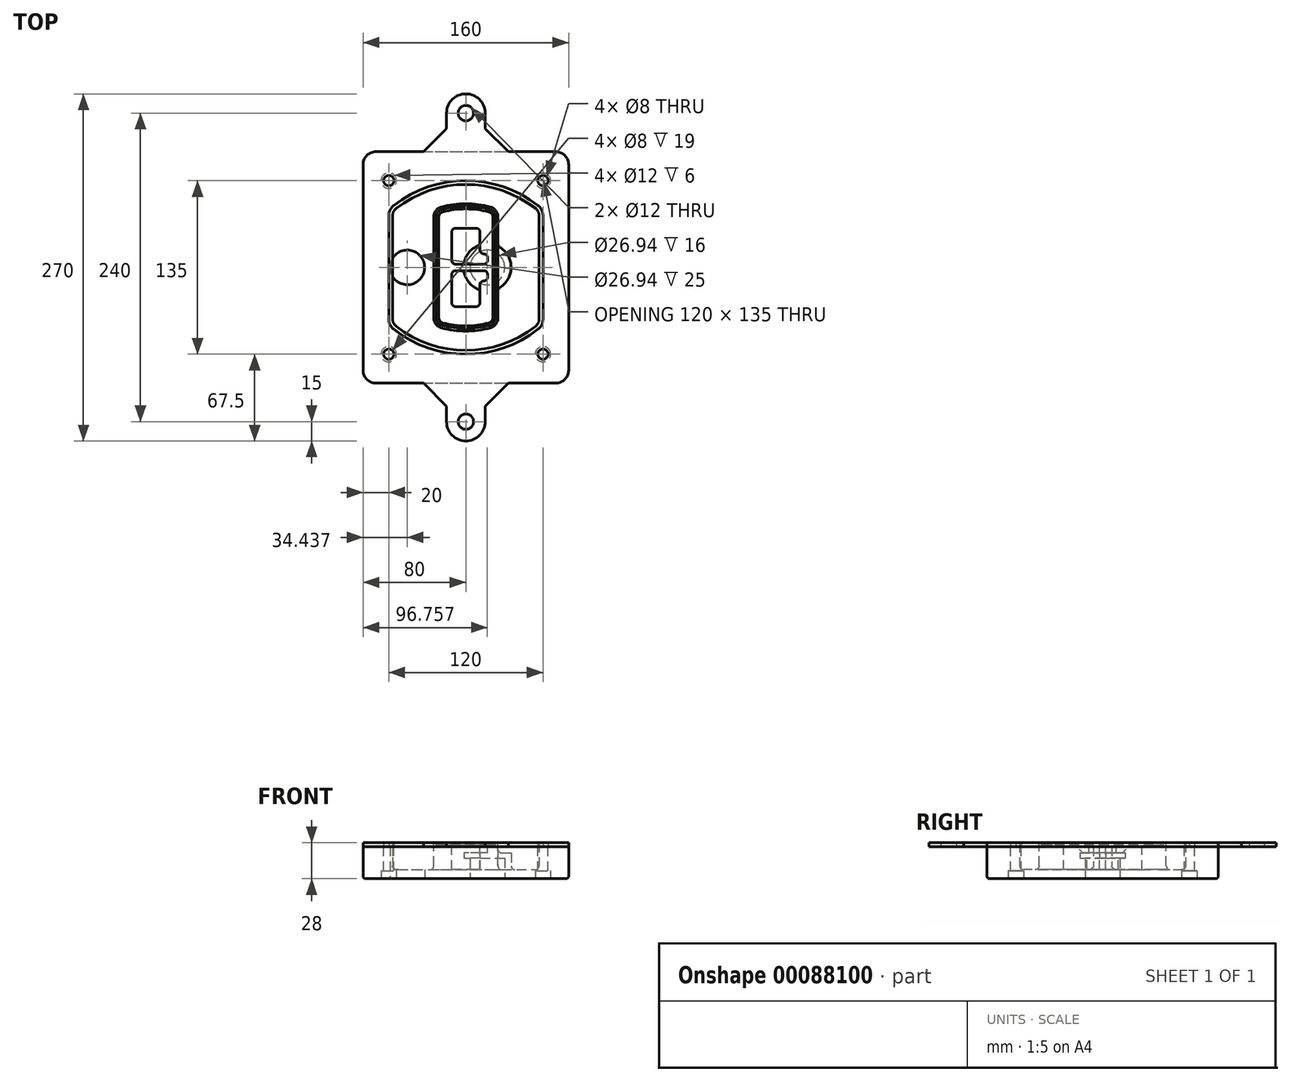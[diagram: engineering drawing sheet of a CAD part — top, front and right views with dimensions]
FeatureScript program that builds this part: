
annotation { "Feature Type Name" : "Feature", "Feature Type Description" : "" }
export const myFeature = defineFeature(function(context is Context, id is Id, definition is map)
    precondition{}
    {
        {
            var Q0;
            Q0=qCreatedBy(makeId("Top.planeOp"),FACE);
            var sketch = newSketch(context, id + "F0", { "sketchPlane" : qUnion([Q0])});
            skPoint(sketch, "E0.rect.middle", {"position": v(0, 0) * mm});
            skLineSegment(sketch, "E1.bottom", {"start": v(-70, -90) * mm, "end": v(70, -90) * mm});
            skLineSegment(sketch, "E1.top", {"start": v(-70, 90) * mm, "end": v(70, 90) * mm});
            skLineSegment(sketch, "E1.left", {"start": v(-80, -80) * mm, "end": v(-80, 80) * mm});
            skLineSegment(sketch, "E1.right", {"start": v(80, -80) * mm, "end": v(80, 80) * mm});
            skLineSegment(sketch, "E2", {"start": v(-80, 90) * mm, "end": v(80, -90) * mm, "construction": true});
            skLineSegment(sketch, "E3", {"start": v(80, 90) * mm, "end": v(-80, -90) * mm, "construction": true});
            skCircle(sketch, "E4", {"center": v(-60, 67.5) * mm, "radius": 4 * mm});
            skCircle(sketch, "E5", {"center": v(60, 67.5) * mm, "radius": 4 * mm});
            skCircle(sketch, "E6", {"center": v(60, -67.5) * mm, "radius": 4 * mm});
            skCircle(sketch, "E7", {"center": v(-60, -67.5) * mm, "radius": 4 * mm});
            skLineSegment(sketch, "E8", {"start": v(-60, 67.5) * mm, "end": v(60, 67.5) * mm, "construction": true});
            skLineSegment(sketch, "E9", {"start": v(60, 67.5) * mm, "end": v(60, -67.5) * mm, "construction": true});
            skLineSegment(sketch, "E10", {"start": v(60, -67.5) * mm, "end": v(-60, -67.5) * mm, "construction": true});
            skLineSegment(sketch, "E11", {"start": v(-60, -67.5) * mm, "end": v(-60, 67.5) * mm, "construction": true});
            skLineSegment(sketch, "E12", {"start": v(-60, 40.3) * mm, "end": v(-60, -40.3) * mm});
            skLineSegment(sketch, "E13", {"start": v(60, 40.3) * mm, "end": v(60, -40.3) * mm});
            skArc(sketch, "E14", {"start": v(56.15, 48.18) * mm, "mid": v(0, 67.5) * mm, "end": v(-56.15, 48.18) * mm});
            skArc(sketch, "E15", {"start": v(-56.15, -48.18) * mm, "mid": v(0, -67.5) * mm, "end": v(56.15, -48.18) * mm});
            skLineSegment(sketch, "E16", {"start": v(-60, 0) * mm, "end": v(60, 0) * mm, "construction": true});
            skPoint(sketch, "E17.visualSharp", {"position": v(-60, -45) * mm});
            skArc(sketch, "E17.filletArc", {"start": v(-60, -40.3) * mm, "mid": v(-58.99, -44.68) * mm, "end": v(-56.15, -48.18) * mm});
            skPoint(sketch, "E18.visualSharp", {"position": v(-60, 45) * mm});
            skArc(sketch, "E18.filletArc", {"start": v(-56.15, 48.18) * mm, "mid": v(-58.99, 44.68) * mm, "end": v(-60, 40.3) * mm});
            skPoint(sketch, "E19.visualSharp", {"position": v(60, 45) * mm});
            skArc(sketch, "E19.filletArc", {"start": v(60, 40.3) * mm, "mid": v(58.99, 44.68) * mm, "end": v(56.15, 48.18) * mm});
            skPoint(sketch, "E20.visualSharp", {"position": v(60, -45) * mm});
            skArc(sketch, "E20.filletArc", {"start": v(56.15, -48.18) * mm, "mid": v(58.99, -44.68) * mm, "end": v(60, -40.3) * mm});
            skPoint(sketch, "E21.visualSharp", {"position": v(-80, 90) * mm});
            skArc(sketch, "E21.filletArc", {"start": v(-70, 90) * mm, "mid": v(-77.07, 87.07) * mm, "end": v(-80, 80) * mm});
            skPoint(sketch, "E22.visualSharp", {"position": v(80, 90) * mm});
            skArc(sketch, "E22.filletArc", {"start": v(80, 80) * mm, "mid": v(77.07, 87.07) * mm, "end": v(70, 90) * mm});
            skPoint(sketch, "E23.visualSharp", {"position": v(80, -90) * mm});
            skArc(sketch, "E23.filletArc", {"start": v(70, -90) * mm, "mid": v(77.07, -87.07) * mm, "end": v(80, -80) * mm});
            skPoint(sketch, "E24.visualSharp", {"position": v(-80, -90) * mm});
            skArc(sketch, "E24.filletArc", {"start": v(-80, -80) * mm, "mid": v(-77.07, -87.07) * mm, "end": v(-70, -90) * mm});
            skArc(sketch, "E25.0", {"start": v(57, 40.3) * mm, "mid": v(56.3, 43.36) * mm, "end": v(54.3, 45.81) * mm});
            skLineSegment(sketch, "E25.1", {"start": v(57, 40.3) * mm, "end": v(57, -40.3) * mm});
            skArc(sketch, "E25.2", {"start": v(54.3, -45.81) * mm, "mid": v(56.3, -43.36) * mm, "end": v(57, -40.3) * mm});
            skArc(sketch, "E25.3", {"start": v(-54.3, -45.81) * mm, "mid": v(0, -64.5) * mm, "end": v(54.3, -45.81) * mm});
            skArc(sketch, "E25.4", {"start": v(-57, -40.3) * mm, "mid": v(-56.3, -43.36) * mm, "end": v(-54.3, -45.81) * mm});
            skArc(sketch, "E25.5", {"start": v(54.3, 45.81) * mm, "mid": v(0, 64.5) * mm, "end": v(-54.3, 45.81) * mm});
            skLineSegment(sketch, "E25.6", {"start": v(-57, 40.3) * mm, "end": v(-57, -40.3) * mm});
            skArc(sketch, "E25.7", {"start": v(-54.3, 45.81) * mm, "mid": v(-56.3, 43.36) * mm, "end": v(-57, 40.3) * mm});
            skArc(sketch, "E26.0", {"start": v(-58.62, 51.33) * mm, "mid": v(-62.58, 46.43) * mm, "end": v(-64, 40.3) * mm});
            skArc(sketch, "E26.1", {"start": v(58.62, 51.33) * mm, "mid": v(0, 71.5) * mm, "end": v(-58.62, 51.33) * mm});
            skArc(sketch, "E26.2", {"start": v(64, 40.3) * mm, "mid": v(62.58, 46.43) * mm, "end": v(58.62, 51.33) * mm});
            skLineSegment(sketch, "E26.3", {"start": v(64, 40.3) * mm, "end": v(64, -40.3) * mm});
            skArc(sketch, "E26.4", {"start": v(58.62, -51.33) * mm, "mid": v(62.58, -46.43) * mm, "end": v(64, -40.3) * mm});
            skLineSegment(sketch, "E26.5", {"start": v(-64, 40.3) * mm, "end": v(-64, -40.3) * mm});
            skArc(sketch, "E26.6", {"start": v(-58.62, -51.33) * mm, "mid": v(0, -71.5) * mm, "end": v(58.62, -51.33) * mm});
            skArc(sketch, "E26.7", {"start": v(-64, -40.3) * mm, "mid": v(-62.58, -46.43) * mm, "end": v(-58.62, -51.33) * mm});
            skSolve(sketch);
        }
        {
            var Q0;
            Q0=makeQuery(id+"F0.imprint","IMPRINT",FACE,{"disambiguationData":[TD([[makeQuery(id+"F0.imprint","IMPRINT",EDGE,{"derivedFrom":sQuery(id+"F0.wireOp",EDGE,"E1.bottom")}),1.0]])]});
            var Q1;
            Q1=makeQuery(id+"F0.imprint","IMPRINT",FACE,{"disambiguationData":[TD([[makeQuery(id+"F0.imprint","IMPRINT",EDGE,{"derivedFrom":sQuery(id+"F0.wireOp",EDGE,"E12")}),1.0]])]});
            var Q2;
            Q2=makeQuery(id+"F0.imprint","IMPRINT",FACE,{"disambiguationData":[TD([[makeQuery(id+"F0.imprint","IMPRINT",EDGE,{"derivedFrom":sQuery(id+"F0.wireOp",EDGE,"E25.0")}),1.0]])]});
            var Q3;
            Q3=makeQuery(id+"F0.imprint","IMPRINT",FACE,{"disambiguationData":[TD([[makeQuery(id+"F0.imprint","IMPRINT",EDGE,{"derivedFrom":sQuery(id+"F0.wireOp",EDGE,"E12")}),-1.0]])]});
            extrude(context, id + "F1", {"entities" : qUnion([Q0, Q1, Q2, Q3]), "oppositeDirection" : true, "depth" : 25 * mm});
        }
        {
            var Q0;
            Q0=makeQuery(id+"F0.imprint","IMPRINT",FACE,{"disambiguationData":[TD([[makeQuery(id+"F0.imprint","IMPRINT",EDGE,{"derivedFrom":sQuery(id+"F0.wireOp",EDGE,"E12")}),1.0]])]});
            extrude(context, id + "F2", {"entities" : qUnion([Q0]), "operationType" : NewBodyOperationType.ADD, "depth" : 3 * mm});
        }
        {
            var Q0;
            Q0=makeQuery(id+"F0.imprint","IMPRINT",FACE,{"disambiguationData":[TD([[makeQuery(id+"F0.imprint","IMPRINT",EDGE,{"derivedFrom":sQuery(id+"F0.wireOp",EDGE,"E25.0")}),1.0]])]});
            extrude(context, id + "F3", {"entities" : qUnion([Q0]), "operationType" : NewBodyOperationType.REMOVE, "oppositeDirection" : true, "depth" : 18 * mm});
        }
        {
            var Q0;
            Q0=makeQuery(id+"F2.opExtrude","CAP_FACE",FACE,{"disambiguationData":[OSD([sQuery(id+"F0.wireOp",EDGE,"E12"),sQuery(id+"F0.wireOp",EDGE,"E13"),sQuery(id+"F0.wireOp",EDGE,"E14"),sQuery(id+"F0.wireOp",EDGE,"E15"),sQuery(id+"F0.wireOp",EDGE,"E17.filletArc"),sQuery(id+"F0.wireOp",EDGE,"E18.filletArc"),sQuery(id+"F0.wireOp",EDGE,"E19.filletArc"),sQuery(id+"F0.wireOp",EDGE,"E20.filletArc"),sQuery(id+"F0.wireOp",EDGE,"E25.0"),sQuery(id+"F0.wireOp",EDGE,"E25.1"),sQuery(id+"F0.wireOp",EDGE,"E25.2"),sQuery(id+"F0.wireOp",EDGE,"E25.3"),sQuery(id+"F0.wireOp",EDGE,"E25.4"),sQuery(id+"F0.wireOp",EDGE,"E25.5"),sQuery(id+"F0.wireOp",EDGE,"E25.6"),sQuery(id+"F0.wireOp",EDGE,"E25.7")])],"isStart":false});
            var sketch = newSketch(context, id + "F4", { "sketchPlane" : qUnion([Q0])});
            skArc(sketch, "E27.0", {"start": v(-19.08, -46.97) * mm, "mid": v(0, -49.5) * mm, "end": v(19.08, -46.97) * mm});
            skArc(sketch, "E28.0", {"start": v(19.08, 46.97) * mm, "mid": v(0, 49.5) * mm, "end": v(-19.08, 46.97) * mm});
            skLineSegment(sketch, "E29", {"start": v(-25, 39.25) * mm, "end": v(-25, -39.25) * mm});
            skLineSegment(sketch, "E30", {"start": v(25, 39.25) * mm, "end": v(25, -39.25) * mm});
            skLineSegment(sketch, "E31", {"start": v(-25, 45.1) * mm, "end": v(25, 45.1) * mm, "construction": true});
            skLineSegment(sketch, "E32", {"start": v(-25, -45.1) * mm, "end": v(25, -45.1) * mm, "construction": true});
            skPoint(sketch, "E33.visualSharp", {"position": v(-25, 45.1) * mm});
            skArc(sketch, "E33.filletArc", {"start": v(-19.08, 46.97) * mm, "mid": v(-23.35, 44.11) * mm, "end": v(-25, 39.25) * mm});
            skPoint(sketch, "E34.visualSharp", {"position": v(25, 45.1) * mm});
            skArc(sketch, "E34.filletArc", {"start": v(25, 39.25) * mm, "mid": v(23.35, 44.11) * mm, "end": v(19.08, 46.97) * mm});
            skPoint(sketch, "E35.visualSharp", {"position": v(25, -45.1) * mm});
            skArc(sketch, "E35.filletArc", {"start": v(19.08, -46.97) * mm, "mid": v(23.35, -44.11) * mm, "end": v(25, -39.25) * mm});
            skPoint(sketch, "E36.visualSharp", {"position": v(-25, -45.1) * mm});
            skArc(sketch, "E36.filletArc", {"start": v(-25, -39.25) * mm, "mid": v(-23.35, -44.11) * mm, "end": v(-19.08, -46.97) * mm});
            skArc(sketch, "E37.0", {"start": v(54.3, 45.81) * mm, "mid": v(0, 64.5) * mm, "end": v(-54.3, 45.81) * mm});
            skArc(sketch, "E37.1", {"start": v(-54.3, 45.81) * mm, "mid": v(-56.3, 43.36) * mm, "end": v(-57, 40.3) * mm});
            skLineSegment(sketch, "E37.2", {"start": v(-57, 40.3) * mm, "end": v(-57, -40.3) * mm});
            skArc(sketch, "E37.3", {"start": v(-57, -40.3) * mm, "mid": v(-56.3, -43.36) * mm, "end": v(-54.3, -45.81) * mm});
            skArc(sketch, "E37.4", {"start": v(-54.3, -45.81) * mm, "mid": v(0, -64.5) * mm, "end": v(54.3, -45.81) * mm});
            skArc(sketch, "E37.5", {"start": v(54.3, -45.81) * mm, "mid": v(56.3, -43.36) * mm, "end": v(57, -40.3) * mm});
            skLineSegment(sketch, "E37.6", {"start": v(57, 40.3) * mm, "end": v(57, -40.3) * mm});
            skArc(sketch, "E37.7", {"start": v(57, 40.3) * mm, "mid": v(56.3, 43.36) * mm, "end": v(54.3, 45.81) * mm});
            skLineSegment(sketch, "E38.0", {"start": v(23, 39.25) * mm, "end": v(23, -39.25) * mm});
            skArc(sketch, "E38.1", {"start": v(18.56, -45.04) * mm, "mid": v(21.76, -42.9) * mm, "end": v(23, -39.25) * mm});
            skArc(sketch, "E38.2", {"start": v(-18.56, -45.04) * mm, "mid": v(0, -47.5) * mm, "end": v(18.56, -45.04) * mm});
            skArc(sketch, "E38.3", {"start": v(-23, -39.25) * mm, "mid": v(-21.76, -42.9) * mm, "end": v(-18.56, -45.04) * mm});
            skLineSegment(sketch, "E38.4", {"start": v(-23, 39.25) * mm, "end": v(-23, -39.25) * mm});
            skArc(sketch, "E38.5", {"start": v(23, 39.25) * mm, "mid": v(21.76, 42.9) * mm, "end": v(18.56, 45.04) * mm});
            skArc(sketch, "E38.6", {"start": v(-18.56, 45.04) * mm, "mid": v(-21.76, 42.9) * mm, "end": v(-23, 39.25) * mm});
            skArc(sketch, "E38.7", {"start": v(18.56, 45.04) * mm, "mid": v(0, 47.5) * mm, "end": v(-18.56, 45.04) * mm});
            skArc(sketch, "E39.0", {"start": v(21, 39.25) * mm, "mid": v(20.18, 41.68) * mm, "end": v(18.04, 43.1) * mm});
            skLineSegment(sketch, "E39.1", {"start": v(21, 39.25) * mm, "end": v(21, -39.25) * mm});
            skArc(sketch, "E39.2", {"start": v(18.04, -43.1) * mm, "mid": v(20.18, -41.68) * mm, "end": v(21, -39.25) * mm});
            skArc(sketch, "E39.3", {"start": v(-18.04, -43.1) * mm, "mid": v(0, -45.5) * mm, "end": v(18.04, -43.1) * mm});
            skArc(sketch, "E39.4", {"start": v(-21, -39.25) * mm, "mid": v(-20.18, -41.68) * mm, "end": v(-18.04, -43.1) * mm});
            skArc(sketch, "E39.5", {"start": v(18.04, 43.1) * mm, "mid": v(0, 45.5) * mm, "end": v(-18.04, 43.1) * mm});
            skLineSegment(sketch, "E39.6", {"start": v(-21, 39.25) * mm, "end": v(-21, -39.25) * mm});
            skArc(sketch, "E39.7", {"start": v(-18.04, 43.1) * mm, "mid": v(-20.18, 41.68) * mm, "end": v(-21, 39.25) * mm});
            skLineSegment(sketch, "E40", {"start": v(-25, 0) * mm, "end": v(25, 0) * mm, "construction": true});
            skLineSegment(sketch, "E41", {"start": v(-11, 5.5) * mm, "end": v(-11, 27.5) * mm});
            skLineSegment(sketch, "E42", {"start": v(-8, 30.5) * mm, "end": v(8, 30.5) * mm});
            skLineSegment(sketch, "E43", {"start": v(11, 27.5) * mm, "end": v(11, 13.5) * mm});
            skLineSegment(sketch, "E44", {"start": v(14, 10.5) * mm, "end": v(14, 10.5) * mm});
            skLineSegment(sketch, "E45", {"start": v(17, 7.5) * mm, "end": v(17, 5.5) * mm});
            skLineSegment(sketch, "E46", {"start": v(14, 2.5) * mm, "end": v(-8, 2.5) * mm});
            skPoint(sketch, "E47.visualSharp", {"position": v(-11, 30.5) * mm});
            skArc(sketch, "E47.filletArc", {"start": v(-8, 30.5) * mm, "mid": v(-10.12, 29.62) * mm, "end": v(-11, 27.5) * mm});
            skPoint(sketch, "E48.visualSharp", {"position": v(11, 30.5) * mm});
            skArc(sketch, "E48.filletArc", {"start": v(11, 27.5) * mm, "mid": v(10.12, 29.62) * mm, "end": v(8, 30.5) * mm});
            skPoint(sketch, "E49.visualSharp", {"position": v(11, 10.5) * mm});
            skArc(sketch, "E49.filletArc", {"start": v(11, 13.5) * mm, "mid": v(11.88, 11.38) * mm, "end": v(14, 10.5) * mm});
            skPoint(sketch, "E50.visualSharp", {"position": v(17, 10.5) * mm});
            skArc(sketch, "E50.filletArc", {"start": v(17, 7.5) * mm, "mid": v(16.12, 9.62) * mm, "end": v(14, 10.5) * mm});
            skPoint(sketch, "E51.visualSharp", {"position": v(17, 2.5) * mm});
            skArc(sketch, "E51.filletArc", {"start": v(14, 2.5) * mm, "mid": v(16.12, 3.38) * mm, "end": v(17, 5.5) * mm});
            skPoint(sketch, "E52.visualSharp", {"position": v(-11, 2.5) * mm});
            skArc(sketch, "E52.filletArc", {"start": v(-11, 5.5) * mm, "mid": v(-10.12, 3.38) * mm, "end": v(-8, 2.5) * mm});
            skLineSegment(sketch, "E53.0.MirrorCS", {"start": v(14, -2.5) * mm, "end": v(-8, -2.5) * mm});
            skArc(sketch, "E54.0.MirrorCS", {"start": v(-11, -5.5) * mm, "mid": v(-10.12, -3.38) * mm, "end": v(-8, -2.5) * mm});
            skLineSegment(sketch, "E55.0.MirrorCS", {"start": v(-11, -5.5) * mm, "end": v(-11, -27.5) * mm});
            skArc(sketch, "E56.0.MirrorCS", {"start": v(-8, -30.5) * mm, "mid": v(-10.12, -29.62) * mm, "end": v(-11, -27.5) * mm});
            skLineSegment(sketch, "E57.0.MirrorCS", {"start": v(-8, -30.5) * mm, "end": v(8, -30.5) * mm});
            skArc(sketch, "E58.0.MirrorCS", {"start": v(11, -27.5) * mm, "mid": v(10.12, -29.62) * mm, "end": v(8, -30.5) * mm});
            skLineSegment(sketch, "E59.0.MirrorCS", {"start": v(11, -27.5) * mm, "end": v(11, -13.5) * mm});
            skArc(sketch, "E60.0.MirrorCS", {"start": v(11, -13.5) * mm, "mid": v(11.88, -11.38) * mm, "end": v(14, -10.5) * mm});
            skArc(sketch, "E61.0.MirrorCS", {"start": v(17, -7.5) * mm, "mid": v(16.12, -9.62) * mm, "end": v(14, -10.5) * mm});
            skLineSegment(sketch, "E62.0.MirrorCS", {"start": v(17, -7.5) * mm, "end": v(17, -5.5) * mm});
            skArc(sketch, "E63.0.MirrorCS", {"start": v(14, -2.5) * mm, "mid": v(16.12, -3.38) * mm, "end": v(17, -5.5) * mm});
            skSolve(sketch);
        }
        {
            var Q0;
            Q0=makeQuery(id+"F4.imprint","IMPRINT",FACE,{"disambiguationData":[TD([[makeQuery(id+"F4.imprint","IMPRINT",EDGE,{"derivedFrom":sQuery(id+"F4.wireOp",EDGE,"E27.0")}),1.0]])]});
            var Q1;
            Q1=makeQuery(id+"F4.imprint","IMPRINT",FACE,{"disambiguationData":[TD([[makeQuery(id+"F4.imprint","IMPRINT",EDGE,{"derivedFrom":sQuery(id+"F4.wireOp",EDGE,"E38.0")}),-1.0]])]});
            var Q2;
            Q2=makeQuery(id+"F4.imprint","IMPRINT",FACE,{"disambiguationData":[TD([[makeQuery(id+"F4.imprint","IMPRINT",EDGE,{"derivedFrom":sQuery(id+"F4.wireOp",EDGE,"E39.0")}),1.0]])]});
            extrude(context, id + "F5", {"entities" : qUnion([Q0, Q1, Q2]), "operationType" : NewBodyOperationType.ADD, "endBound" : BoundingType.UP_TO_NEXT, "oppositeDirection" : true, "depth" : 25 * mm});
        }
        {
            var Q0;
            Q0=makeQuery(id+"F4.imprint","IMPRINT",FACE,{"disambiguationData":[TD([[makeQuery(id+"F4.imprint","IMPRINT",EDGE,{"derivedFrom":sQuery(id+"F4.wireOp",EDGE,"E38.0")}),-1.0]])]});
            extrude(context, id + "F6", {"entities" : qUnion([Q0]), "operationType" : NewBodyOperationType.REMOVE, "oppositeDirection" : true, "depth" : 2 * mm});
        }
        {
            var Q0;
            Q0=makeQuery(id+"F1.opExtrude","CAP_FACE",FACE,{"disambiguationData":[OSD([sQuery(id+"F0.wireOp",EDGE,"E1.bottom"),sQuery(id+"F0.wireOp",EDGE,"E1.top"),sQuery(id+"F0.wireOp",EDGE,"E1.left"),sQuery(id+"F0.wireOp",EDGE,"E1.right"),sQuery(id+"F0.wireOp",EDGE,"E4"),sQuery(id+"F0.wireOp",EDGE,"E5"),sQuery(id+"F0.wireOp",EDGE,"E6"),sQuery(id+"F0.wireOp",EDGE,"E7"),sQuery(id+"F0.wireOp",EDGE,"E21.filletArc"),sQuery(id+"F0.wireOp",EDGE,"E22.filletArc"),sQuery(id+"F0.wireOp",EDGE,"E23.filletArc"),sQuery(id+"F0.wireOp",EDGE,"E24.filletArc")])],"isStart":false});
            var sketch = newSketch(context, id + "F7", { "sketchPlane" : qUnion([Q0])});
            skCircle(sketch, "E64", {"center": v(16.76, 0) * mm, "radius": 13.47 * mm});
            skCircle(sketch, "E65", {"center": v(-45.56, 0) * mm, "radius": 13.47 * mm});
            skLineSegment(sketch, "E66", {"start": v(80, 0) * mm, "end": v(-80, 0) * mm});
            skCircle(sketch, "E67", {"center": v(16.76, 0) * mm, "radius": 18.47 * mm});
            skCircle(sketch, "E68", {"center": v(60, -67.5) * mm, "radius": 6 * mm});
            skCircle(sketch, "E69", {"center": v(-60, -67.5) * mm, "radius": 6 * mm});
            skCircle(sketch, "E70", {"center": v(-60, 67.5) * mm, "radius": 6 * mm});
            skCircle(sketch, "E71", {"center": v(60, 67.5) * mm, "radius": 6 * mm});
            skSolve(sketch);
        }
        {
            var Q0;
            {var subQ1=sQuery(id+"F7.wireOp",EDGE,"E66");var subQ4=sQuery(id+"F7.wireOp",EDGE,"E64");var subQ6=makeQuery(id+"F7.imprint","INTERSECT",VERTEX,{"disambiguationData":[OD(0.0)],"derivedFrom":[subQ4,subQ1]});Q0=makeQuery(id+"F7.imprint","IMPRINT",FACE,{"disambiguationData":[TD([[makeQuery(id+"F7.imprint","IMPRINT",EDGE,{"disambiguationData":[TD([[subQ6,-1.0]])],"derivedFrom":subQ4}),-1.0]])]});}
            var Q1;
            {var subQ0=sQuery(id+"F7.wireOp",EDGE,"E66");var subQ1=sQuery(id+"F7.wireOp",EDGE,"E64");var subQ3=makeQuery(id+"F7.imprint","INTERSECT",VERTEX,{"disambiguationData":[OD(0.0)],"derivedFrom":[subQ1,subQ0]});Q1=makeQuery(id+"F7.imprint","IMPRINT",FACE,{"disambiguationData":[TD([[makeQuery(id+"F7.imprint","IMPRINT",EDGE,{"disambiguationData":[TD([[subQ3,-1.0]])],"derivedFrom":subQ1}),1.0]])]});}
            var Q2;
            {var subQ0=sQuery(id+"F7.wireOp",EDGE,"E66");var subQ1=sQuery(id+"F7.wireOp",EDGE,"E64");var subQ3=makeQuery(id+"F7.imprint","INTERSECT",VERTEX,{"disambiguationData":[OD(0.0)],"derivedFrom":[subQ1,subQ0]});Q2=makeQuery(id+"F7.imprint","IMPRINT",FACE,{"disambiguationData":[TD([[makeQuery(id+"F7.imprint","IMPRINT",EDGE,{"disambiguationData":[TD([[subQ3,1.0]])],"derivedFrom":subQ1}),1.0]])]});}
            var Q3;
            {var subQ1=sQuery(id+"F7.wireOp",EDGE,"E66");var subQ4=sQuery(id+"F7.wireOp",EDGE,"E64");var subQ6=makeQuery(id+"F7.imprint","INTERSECT",VERTEX,{"disambiguationData":[OD(0.0)],"derivedFrom":[subQ4,subQ1]});Q3=makeQuery(id+"F7.imprint","IMPRINT",FACE,{"disambiguationData":[TD([[makeQuery(id+"F7.imprint","IMPRINT",EDGE,{"disambiguationData":[TD([[subQ6,1.0]])],"derivedFrom":subQ4}),-1.0]])]});}
            extrude(context, id + "F8", {"entities" : qUnion([Q0, Q1, Q2, Q3]), "operationType" : NewBodyOperationType.ADD, "oppositeDirection" : true, "depth" : 20 * mm});
        }
        {
            var Q0;
            {var subQ0=sQuery(id+"F7.wireOp",EDGE,"E66");var subQ1=sQuery(id+"F7.wireOp",EDGE,"E64");var subQ3=makeQuery(id+"F7.imprint","INTERSECT",VERTEX,{"disambiguationData":[OD(0.0)],"derivedFrom":[subQ1,subQ0]});Q0=makeQuery(id+"F7.imprint","IMPRINT",FACE,{"disambiguationData":[TD([[makeQuery(id+"F7.imprint","IMPRINT",EDGE,{"disambiguationData":[TD([[subQ3,-1.0]])],"derivedFrom":subQ1}),1.0]])]});}
            var Q1;
            {var subQ0=sQuery(id+"F7.wireOp",EDGE,"E66");var subQ1=sQuery(id+"F7.wireOp",EDGE,"E64");var subQ3=makeQuery(id+"F7.imprint","INTERSECT",VERTEX,{"disambiguationData":[OD(0.0)],"derivedFrom":[subQ1,subQ0]});Q1=makeQuery(id+"F7.imprint","IMPRINT",FACE,{"disambiguationData":[TD([[makeQuery(id+"F7.imprint","IMPRINT",EDGE,{"disambiguationData":[TD([[subQ3,1.0]])],"derivedFrom":subQ1}),1.0]])]});}
            extrude(context, id + "F9", {"entities" : qUnion([Q0, Q1]), "operationType" : NewBodyOperationType.REMOVE, "oppositeDirection" : true, "depth" : 16 * mm});
        }
        {
            var Q0;
            {var subQ0=sQuery(id+"F7.wireOp",EDGE,"E66");var subQ1=sQuery(id+"F7.wireOp",EDGE,"E65");var subQ3=makeQuery(id+"F7.imprint","INTERSECT",VERTEX,{"disambiguationData":[OD(0.0)],"derivedFrom":[subQ1,subQ0]});Q0=makeQuery(id+"F7.imprint","IMPRINT",FACE,{"disambiguationData":[TD([[makeQuery(id+"F7.imprint","IMPRINT",EDGE,{"disambiguationData":[TD([[subQ3,-1.0]])],"derivedFrom":subQ1}),1.0]])]});}
            var Q1;
            {var subQ0=sQuery(id+"F7.wireOp",EDGE,"E66");var subQ1=sQuery(id+"F7.wireOp",EDGE,"E65");var subQ3=makeQuery(id+"F7.imprint","INTERSECT",VERTEX,{"disambiguationData":[OD(0.0)],"derivedFrom":[subQ1,subQ0]});Q1=makeQuery(id+"F7.imprint","IMPRINT",FACE,{"disambiguationData":[TD([[makeQuery(id+"F7.imprint","IMPRINT",EDGE,{"disambiguationData":[TD([[subQ3,1.0]])],"derivedFrom":subQ1}),1.0]])]});}
            extrude(context, id + "F10", {"entities" : qUnion([Q0, Q1]), "operationType" : NewBodyOperationType.REMOVE, "oppositeDirection" : true, "depth" : 25 * mm});
        }
        {
            var Q0;
            Q0=makeQuery(id+"F7.imprint","IMPRINT",FACE,{"disambiguationData":[TD([[makeQuery(id+"F7.imprint","IMPRINT",EDGE,{"derivedFrom":sQuery(id+"F7.wireOp",EDGE,"E68")}),1.0]])]});
            var Q1;
            Q1=makeQuery(id+"F7.imprint","IMPRINT",FACE,{"disambiguationData":[TD([[makeQuery(id+"F7.imprint","IMPRINT",EDGE,{"derivedFrom":makeQuery(id+"F1.opExtrude","CAP_EDGE",EDGE,{"disambiguationData":[OSD([sQuery(id+"F0.wireOp",EDGE,"E5")])],"isStart":false})}),-1.0]])]});
            var Q2;
            Q2=makeQuery(id+"F7.imprint","IMPRINT",FACE,{"disambiguationData":[TD([[makeQuery(id+"F7.imprint","IMPRINT",EDGE,{"derivedFrom":sQuery(id+"F7.wireOp",EDGE,"E69")}),1.0]])]});
            var Q3;
            Q3=makeQuery(id+"F7.imprint","IMPRINT",FACE,{"disambiguationData":[TD([[makeQuery(id+"F7.imprint","IMPRINT",EDGE,{"derivedFrom":makeQuery(id+"F1.opExtrude","CAP_EDGE",EDGE,{"disambiguationData":[OSD([sQuery(id+"F0.wireOp",EDGE,"E4")])],"isStart":false})}),-1.0]])]});
            var Q4;
            Q4=makeQuery(id+"F7.imprint","IMPRINT",FACE,{"disambiguationData":[TD([[makeQuery(id+"F7.imprint","IMPRINT",EDGE,{"derivedFrom":sQuery(id+"F7.wireOp",EDGE,"E70")}),1.0]])]});
            var Q5;
            Q5=makeQuery(id+"F7.imprint","IMPRINT",FACE,{"disambiguationData":[TD([[makeQuery(id+"F7.imprint","IMPRINT",EDGE,{"derivedFrom":makeQuery(id+"F1.opExtrude","CAP_EDGE",EDGE,{"disambiguationData":[OSD([sQuery(id+"F0.wireOp",EDGE,"E7")])],"isStart":false})}),-1.0]])]});
            var Q6;
            Q6=makeQuery(id+"F7.imprint","IMPRINT",FACE,{"disambiguationData":[TD([[makeQuery(id+"F7.imprint","IMPRINT",EDGE,{"derivedFrom":sQuery(id+"F7.wireOp",EDGE,"E71")}),1.0]])]});
            var Q7;
            Q7=makeQuery(id+"F7.imprint","IMPRINT",FACE,{"disambiguationData":[TD([[makeQuery(id+"F7.imprint","IMPRINT",EDGE,{"derivedFrom":makeQuery(id+"F1.opExtrude","CAP_EDGE",EDGE,{"disambiguationData":[OSD([sQuery(id+"F0.wireOp",EDGE,"E6")])],"isStart":false})}),-1.0]])]});
            extrude(context, id + "F11", {"entities" : qUnion([Q0, Q1, Q2, Q3, Q4, Q5, Q6, Q7]), "operationType" : NewBodyOperationType.REMOVE, "oppositeDirection" : true, "depth" : 6 * mm});
        }
        {
            var Q0;
            Q0=makeQuery(id+"F9.boolean.opBoolean","COPY",FACE,{"derivedFrom":makeQuery(id+"F9.opExtrude","CAP_FACE",FACE,{"disambiguationData":[OSD([sQuery(id+"F7.wireOp",EDGE,"E64")])],"isStart":false})});
            var sketch = newSketch(context, id + "F12", { "sketchPlane" : qUnion([Q0])});
            skArc(sketch, "E72.0", {"start": v(11, 17.55) * mm, "mid": v(2.57, 11.82) * mm, "end": v(-1.54, 2.5) * mm});
            skArc(sketch, "E72.1", {"start": v(-1.54, -2.5) * mm, "mid": v(2.57, -11.82) * mm, "end": v(11, -17.55) * mm});
            skLineSegment(sketch, "E73", {"start": v(-1.54, -2.5) * mm, "end": v(14, -2.5) * mm});
            skLineSegment(sketch, "E74.0", {"start": v(14, 2.5) * mm, "end": v(-1.54, 2.5) * mm});
            skArc(sketch, "E74.1", {"start": v(14, 2.5) * mm, "mid": v(16.12, 3.38) * mm, "end": v(17, 5.5) * mm});
            skLineSegment(sketch, "E74.2", {"start": v(17, 7.5) * mm, "end": v(17, 5.5) * mm});
            skArc(sketch, "E74.3", {"start": v(17, 7.5) * mm, "mid": v(16.12, 9.62) * mm, "end": v(14, 10.5) * mm});
            skArc(sketch, "E74.4", {"start": v(11, 13.5) * mm, "mid": v(11.88, 11.38) * mm, "end": v(14, 10.5) * mm});
            skLineSegment(sketch, "E74.5", {"start": v(11, 17.55) * mm, "end": v(11, 13.5) * mm});
            skLineSegment(sketch, "E74.7", {"start": v(14, -2.5) * mm, "end": v(-1.54, -2.5) * mm});
            skArc(sketch, "E74.8", {"start": v(14, -2.5) * mm, "mid": v(16.12, -3.38) * mm, "end": v(17, -5.5) * mm});
            skLineSegment(sketch, "E74.9", {"start": v(17, -7.5) * mm, "end": v(17, -5.5) * mm});
            skArc(sketch, "E74.10", {"start": v(17, -7.5) * mm, "mid": v(16.12, -9.62) * mm, "end": v(14, -10.5) * mm});
            skArc(sketch, "E74.11", {"start": v(11, -13.5) * mm, "mid": v(11.88, -11.38) * mm, "end": v(14, -10.5) * mm});
            skLineSegment(sketch, "E74.12", {"start": v(11, -17.55) * mm, "end": v(11, -13.5) * mm});
            skPoint(sketch, "E75.orphan", {"position": v(11, -27.5) * mm});
            skPoint(sketch, "E76.orphan", {"position": v(-8, -2.5) * mm});
            skPoint(sketch, "E77.orphan", {"position": v(-8, 2.5) * mm});
            skPoint(sketch, "E78.orphan", {"position": v(11, 27.5) * mm});
            skSolve(sketch);
        }
        {
            var Q0;
            {var subQ7=sQuery(id+"F12.wireOp",EDGE,"E72.0");var subQ14=sQuery(id+"F12.wireOp",EDGE,"E72.1");var subQ16=sQuery(id+"F12.wireOp",EDGE,"E74.1");var subQ18=sQuery(id+"F12.wireOp",EDGE,"E74.8");Q0=qUnion([makeQuery(id+"F12.imprint","IMPRINT",FACE,{"disambiguationData":[TD([[makeQuery(id+"F12.imprint","IMPRINT",EDGE,{"derivedFrom":subQ7}),1.0]])]}),makeQuery(id+"F12.imprint","IMPRINT",FACE,{"disambiguationData":[TD([[makeQuery(id+"F12.imprint","IMPRINT",EDGE,{"derivedFrom":subQ14}),1.0]])]}),makeQuery(id+"F12.imprint","IMPRINT",FACE,{"disambiguationData":[TD([[makeQuery(id+"F12.imprint","IMPRINT",EDGE,{"derivedFrom":subQ16}),1.0]])]}),makeQuery(id+"F12.imprint","IMPRINT",FACE,{"disambiguationData":[TD([[makeQuery(id+"F12.imprint","IMPRINT",EDGE,{"derivedFrom":subQ18}),-1.0]])]})]);}
            var Q1;
            Q1=makeQuery(id+"F5.boolean.opBoolean","SPLIT",FACE,{"disambiguationData":[TD([makeQuery(id+"F5.opExtrude","SWEPT_FACE",FACE,{"disambiguationData":[OSD([sQuery(id+"F4.wireOp",EDGE,"E41")])]})])],"derivedFrom":makeQuery(id+"F3.boolean.opBoolean","COPY",FACE,{"derivedFrom":makeQuery(id+"F3.opExtrude","CAP_FACE",FACE,{"disambiguationData":[OSD([sQuery(id+"F0.wireOp",EDGE,"E25.0"),sQuery(id+"F0.wireOp",EDGE,"E25.1"),sQuery(id+"F0.wireOp",EDGE,"E25.2"),sQuery(id+"F0.wireOp",EDGE,"E25.3"),sQuery(id+"F0.wireOp",EDGE,"E25.4"),sQuery(id+"F0.wireOp",EDGE,"E25.5"),sQuery(id+"F0.wireOp",EDGE,"E25.6"),sQuery(id+"F0.wireOp",EDGE,"E25.7")])],"isStart":false})})});
            extrude(context, id + "F13", {"entities" : qUnion([Q0]), "operationType" : NewBodyOperationType.REMOVE, "endBound" : BoundingType.UP_TO_SURFACE, "endBoundEntityFace" : qUnion([Q1]), "depth" : 25 * mm});
        }
        {
            var Q0;
            Q0=makeQuery(id+"F3.boolean.opBoolean","COPY",EDGE,{"derivedFrom":makeQuery(id+"F3.opExtrude","CAP_EDGE",EDGE,{"disambiguationData":[OSD([sQuery(id+"F0.wireOp",EDGE,"E25.6")])],"isStart":false})});
            var Q1;
            Q1=makeQuery(id+"F8.boolean.opBoolean","INTERSECT",EDGE,{"derivedFrom":[makeQuery(id+"F5.opExtrude","SWEPT_FACE",FACE,{"disambiguationData":[OSD([sQuery(id+"F4.wireOp",EDGE,"E30")])]}),makeQuery(id+"F8.opExtrude","CAP_FACE",FACE,{"disambiguationData":[OSD([sQuery(id+"F7.wireOp",EDGE,"E67")])],"isStart":false})]});
            var Q2;
            Q2=makeQuery(id+"F8.boolean.opBoolean","INTERSECT",EDGE,{"disambiguationData":[OD(1.0)],"derivedFrom":[makeQuery(id+"F5.opExtrude","SWEPT_FACE",FACE,{"disambiguationData":[OSD([sQuery(id+"F4.wireOp",EDGE,"E30")])]}),makeQuery(id+"F8.opExtrude","SWEPT_FACE",FACE,{"disambiguationData":[OSD([sQuery(id+"F7.wireOp",EDGE,"E67")])]})]});
            var Q3;
            {var subQ0=sQuery(id+"F4.wireOp",EDGE,"E30");Q3=makeQuery(id+"F8.boolean.opBoolean","SPLIT",EDGE,{"disambiguationData":[TD([makeQuery(id+"F5.opExtrude","SWEPT_FACE",FACE,{"disambiguationData":[OSD([sQuery(id+"F4.wireOp",EDGE,"E35.filletArc")])]})])],"derivedFrom":makeQuery(id+"F5.opExtrude","CAP_EDGE",EDGE,{"disambiguationData":[OSD([subQ0])],"isStart":false})});}
            var Q4;
            {var subQ0=sQuery(id+"F0.wireOp",EDGE,"E25.7");var subQ1=sQuery(id+"F0.wireOp",EDGE,"E25.1");var subQ2=sQuery(id+"F0.wireOp",EDGE,"E25.6");var subQ3=sQuery(id+"F0.wireOp",EDGE,"E25.5");var subQ4=sQuery(id+"F0.wireOp",EDGE,"E25.4");var subQ5=sQuery(id+"F0.wireOp",EDGE,"E25.0");var subQ6=sQuery(id+"F0.wireOp",EDGE,"E25.2");var subQ7=sQuery(id+"F0.wireOp",EDGE,"E25.3");Q4=makeQuery(id+"F8.boolean.opBoolean","INTERSECT",EDGE,{"derivedFrom":[makeQuery(id+"F5.boolean.opBoolean","SPLIT",FACE,{"disambiguationData":[TD([makeQuery(id+"F2.opExtrude","SWEPT_FACE",FACE,{"disambiguationData":[OSD([subQ5])]})])],"derivedFrom":makeQuery(id+"F3.boolean.opBoolean","COPY",FACE,{"derivedFrom":makeQuery(id+"F3.opExtrude","CAP_FACE",FACE,{"disambiguationData":[OSD([subQ5,subQ1,subQ6,subQ7,subQ4,subQ3,subQ2,subQ0])],"isStart":false})})}),makeQuery(id+"F8.opExtrude","SWEPT_FACE",FACE,{"disambiguationData":[OSD([sQuery(id+"F7.wireOp",EDGE,"E67")])]})]});}
            var Q5;
            Q5=makeQuery(id+"F8.boolean.opBoolean","INTERSECT",EDGE,{"disambiguationData":[OD(0.0)],"derivedFrom":[makeQuery(id+"F5.opExtrude","SWEPT_FACE",FACE,{"disambiguationData":[OSD([sQuery(id+"F4.wireOp",EDGE,"E30")])]}),makeQuery(id+"F8.opExtrude","SWEPT_FACE",FACE,{"disambiguationData":[OSD([sQuery(id+"F7.wireOp",EDGE,"E67")])]})]});
            fillet(context, id + "F14", {"entities" : qUnion([Q0, Q1, Q2, Q3, Q4, Q5]), "radius" : 3 * mm, "tangentPropagation" : true, "allowEdgeOverflow" : false});
        }
        {
            var Q0;
            Q0=makeQuery(id+"F1.opExtrude","CAP_EDGE",EDGE,{"disambiguationData":[OSD([sQuery(id+"F0.wireOp",EDGE,"E1.bottom")])],"isStart":false});
            fillet(context, id + "F15", {"entities" : qUnion([Q0]), "radius" : 2 * mm, "tangentPropagation" : true, "allowEdgeOverflow" : false});
        }
        {
            var Q0;
            {var subQ0=sQuery(id+"F0.wireOp",EDGE,"E22.filletArc");var subQ1=sQuery(id+"F0.wireOp",EDGE,"E7");var subQ2=sQuery(id+"F0.wireOp",EDGE,"E6");var subQ3=sQuery(id+"F0.wireOp",EDGE,"E5");var subQ4=sQuery(id+"F0.wireOp",EDGE,"E4");var subQ5=sQuery(id+"F0.wireOp",EDGE,"E1.bottom");var subQ6=sQuery(id+"F0.wireOp",EDGE,"E21.filletArc");var subQ7=sQuery(id+"F0.wireOp",EDGE,"E1.top");var subQ8=sQuery(id+"F0.wireOp",EDGE,"E1.left");var subQ9=sQuery(id+"F0.wireOp",EDGE,"E1.right");var subQ10=sQuery(id+"F0.wireOp",EDGE,"E23.filletArc");var subQ11=sQuery(id+"F0.wireOp",EDGE,"E24.filletArc");Q0=makeQuery(id+"F2.boolean.opBoolean","SPLIT",FACE,{"disambiguationData":[TD([makeQuery(id+"F1.opExtrude","SWEPT_FACE",FACE,{"disambiguationData":[OSD([subQ5])]})])],"derivedFrom":makeQuery(id+"F1.opExtrude","CAP_FACE",FACE,{"disambiguationData":[OSD([subQ5,subQ7,subQ8,subQ9,subQ4,subQ3,subQ2,subQ1,subQ6,subQ0,subQ10,subQ11])],"isStart":true})});}
            var sketch = newSketch(context, id + "F16", { "sketchPlane" : qUnion([Q0])});
            skLineSegment(sketch, "E79.0", {"start": v(-60, 40.3) * mm, "end": v(-60, -40.3) * mm});
            skArc(sketch, "E79.1", {"start": v(-56.15, 48.18) * mm, "mid": v(-58.99, 44.68) * mm, "end": v(-60, 40.3) * mm});
            skArc(sketch, "E79.2", {"start": v(56.15, 48.18) * mm, "mid": v(0, 67.5) * mm, "end": v(-56.15, 48.18) * mm});
            skArc(sketch, "E79.3", {"start": v(60, 40.3) * mm, "mid": v(58.99, 44.68) * mm, "end": v(56.15, 48.18) * mm});
            skLineSegment(sketch, "E79.4", {"start": v(60, 40.3) * mm, "end": v(60, -40.3) * mm});
            skArc(sketch, "E79.5", {"start": v(56.15, -48.18) * mm, "mid": v(58.99, -44.68) * mm, "end": v(60, -40.3) * mm});
            skArc(sketch, "E79.6", {"start": v(-56.15, -48.18) * mm, "mid": v(0, -67.5) * mm, "end": v(56.15, -48.18) * mm});
            skArc(sketch, "E79.7", {"start": v(-60, -40.3) * mm, "mid": v(-58.99, -44.68) * mm, "end": v(-56.15, -48.18) * mm});
            skCircle(sketch, "E79.10", {"center": v(60, -67.5) * mm, "radius": 4 * mm});
            skLineSegment(sketch, "E79.12", {"start": v(-70, -90) * mm, "end": v(70, -90) * mm});
            skArc(sketch, "E79.13", {"start": v(-80, -80) * mm, "mid": v(-77.07, -87.07) * mm, "end": v(-70, -90) * mm});
            skLineSegment(sketch, "E79.14", {"start": v(-80, -80) * mm, "end": v(-80, 80) * mm});
            skArc(sketch, "E79.15", {"start": v(-70, 90) * mm, "mid": v(-77.07, 87.07) * mm, "end": v(-80, 80) * mm});
            skLineSegment(sketch, "E79.16", {"start": v(70, 90) * mm, "end": v(-70, 90) * mm});
            skArc(sketch, "E79.17", {"start": v(80, 80) * mm, "mid": v(77.07, 87.07) * mm, "end": v(70, 90) * mm});
            skLineSegment(sketch, "E79.18", {"start": v(80, -80) * mm, "end": v(80, 80) * mm});
            skArc(sketch, "E79.19", {"start": v(70, -90) * mm, "mid": v(77.07, -87.07) * mm, "end": v(80, -80) * mm});
            skCircle(sketch, "E80.0", {"center": v(-60, -67.5) * mm, "radius": 4 * mm});
            skCircle(sketch, "E80.1", {"center": v(-60, 67.5) * mm, "radius": 4 * mm});
            skCircle(sketch, "E80.2", {"center": v(60, 67.5) * mm, "radius": 4 * mm});
            skLineSegment(sketch, "E81", {"start": v(-33, 90) * mm, "end": v(-15, 108) * mm});
            skLineSegment(sketch, "E82", {"start": v(-15, 108) * mm, "end": v(-15, 120) * mm});
            skLineSegment(sketch, "E83", {"start": v(33, 90) * mm, "end": v(15, 108) * mm});
            skLineSegment(sketch, "E84", {"start": v(15, 108) * mm, "end": v(15, 120) * mm});
            skCircle(sketch, "E85", {"center": v(0, 120) * mm, "radius": 6 * mm});
            skArc(sketch, "E86", {"start": v(15, 120) * mm, "mid": v(0, 135) * mm, "end": v(-15, 120) * mm});
            skLineSegment(sketch, "E87", {"start": v(0, 120) * mm, "end": v(0, 90) * mm, "construction": true});
            skLineSegment(sketch, "E88", {"start": v(33, 90) * mm, "end": v(-33, 90) * mm});
            skPoint(sketch, "E89.endSnap0", {"position": v(60, 0) * mm});
            skLineSegment(sketch, "E90", {"start": v(-80, 0) * mm, "end": v(80, 0) * mm, "construction": true});
            skLineSegment(sketch, "E91.MirrorCS", {"start": v(-33, -90) * mm, "end": v(-15, -108) * mm});
            skLineSegment(sketch, "E92.MirrorCS", {"start": v(-15, -108) * mm, "end": v(-15, -120) * mm});
            skArc(sketch, "E93.MirrorCS", {"start": v(15, -120) * mm, "mid": v(0, -135) * mm, "end": v(-15, -120) * mm});
            skLineSegment(sketch, "E94.MirrorCS", {"start": v(15, -108) * mm, "end": v(15, -120) * mm});
            skLineSegment(sketch, "E95.MirrorCS", {"start": v(33, -90) * mm, "end": v(15, -108) * mm});
            skCircle(sketch, "E96.MirrorC", {"center": v(0, -120) * mm, "radius": 6 * mm});
            skLineSegment(sketch, "E97.MirrorCS", {"start": v(0, -120) * mm, "end": v(0, -90) * mm, "construction": true});
            skSolve(sketch);
        }
        {
            var Q0;
            Q0=makeQuery(id+"F16.imprint","IMPRINT",FACE,{"disambiguationData":[TD([[makeQuery(id+"F16.imprint","IMPRINT",EDGE,{"derivedFrom":sQuery(id+"F16.wireOp",EDGE,"E81")}),-1.0]])]});
            var Q1;
            Q1=makeQuery(id+"F16.imprint","IMPRINT",FACE,{"disambiguationData":[TD([[makeQuery(id+"F16.imprint","IMPRINT",EDGE,{"derivedFrom":sQuery(id+"F16.wireOp",EDGE,"E79.0")}),-1.0]])]});
            var Q2;
            {var subQ0=sQuery(id+"F16.wireOp",EDGE,"E91.MirrorCS");Q2=makeQuery(id+"F16.imprint","IMPRINT",FACE,{"disambiguationData":[TD([[makeQuery(id+"F16.imprint","IMPRINT",EDGE,{"derivedFrom":subQ0}),1.0]])]});}
            var Q3;
            Q3=makeQuery(id+"F2.opExtrude","CAP_FACE",FACE,{"disambiguationData":[OSD([sQuery(id+"F0.wireOp",EDGE,"E12"),sQuery(id+"F0.wireOp",EDGE,"E13"),sQuery(id+"F0.wireOp",EDGE,"E14"),sQuery(id+"F0.wireOp",EDGE,"E15"),sQuery(id+"F0.wireOp",EDGE,"E17.filletArc"),sQuery(id+"F0.wireOp",EDGE,"E18.filletArc"),sQuery(id+"F0.wireOp",EDGE,"E19.filletArc"),sQuery(id+"F0.wireOp",EDGE,"E20.filletArc"),sQuery(id+"F0.wireOp",EDGE,"E25.0"),sQuery(id+"F0.wireOp",EDGE,"E25.1"),sQuery(id+"F0.wireOp",EDGE,"E25.2"),sQuery(id+"F0.wireOp",EDGE,"E25.3"),sQuery(id+"F0.wireOp",EDGE,"E25.4"),sQuery(id+"F0.wireOp",EDGE,"E25.5"),sQuery(id+"F0.wireOp",EDGE,"E25.6"),sQuery(id+"F0.wireOp",EDGE,"E25.7")])],"isStart":false});
            extrude(context, id + "F17", {"entities" : qUnion([Q0, Q1, Q2]), "endBound" : BoundingType.UP_TO_SURFACE, "endBoundEntityFace" : qUnion([Q3]), "depth" : 25 * mm});
        }
    });
